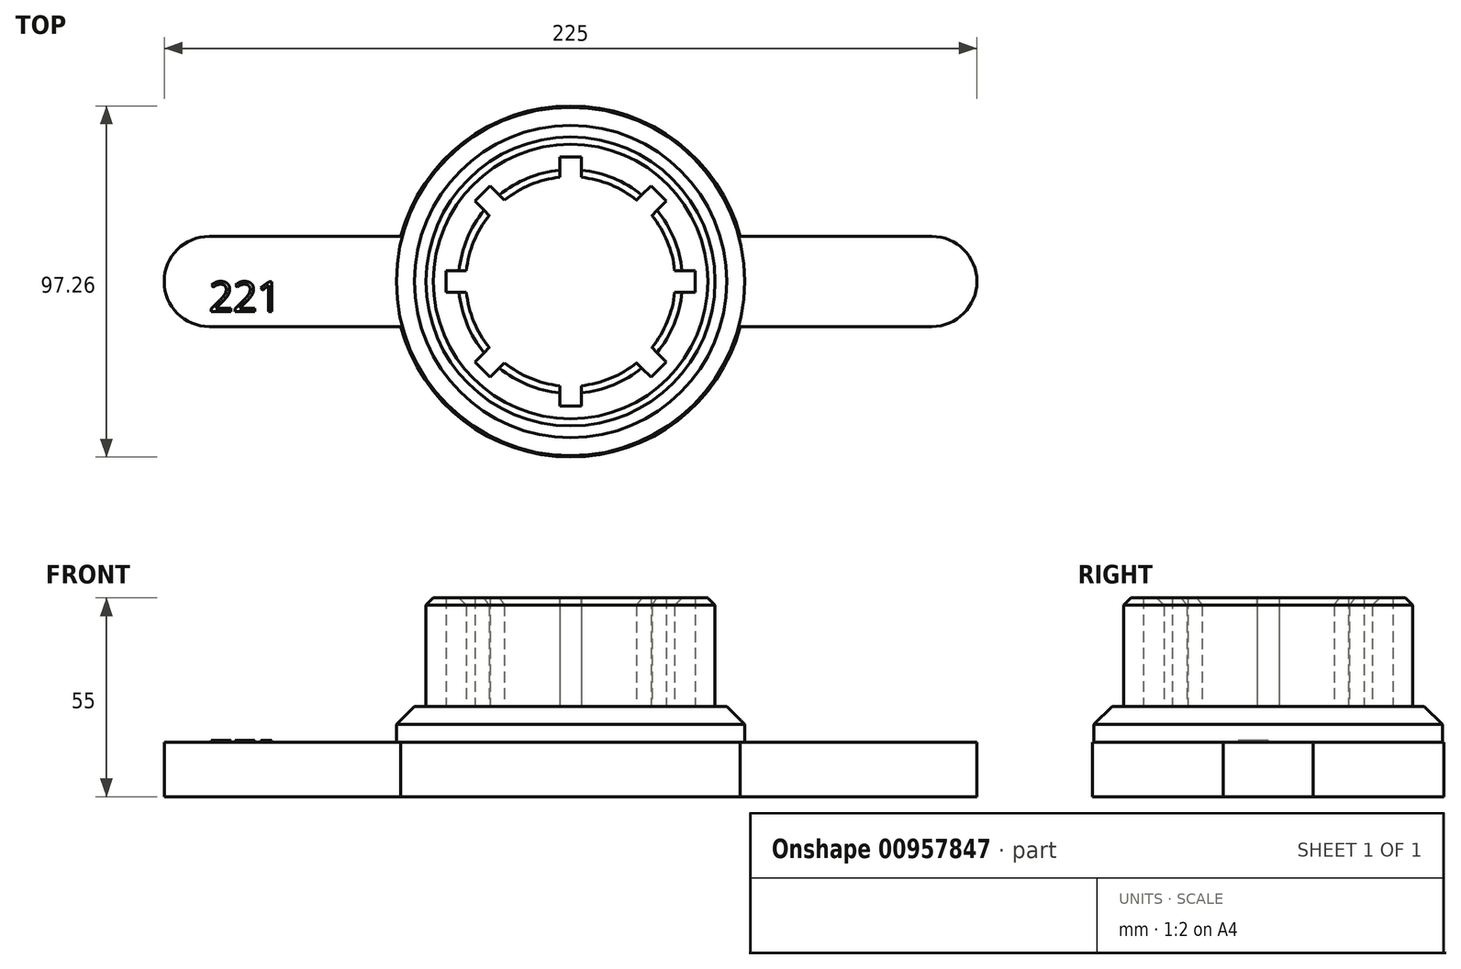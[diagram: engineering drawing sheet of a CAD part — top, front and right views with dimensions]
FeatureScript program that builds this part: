
annotation { "Feature Type Name" : "Feature", "Feature Type Description" : "" }
export const myFeature = defineFeature(function(context is Context, id is Id, definition is map)
    precondition{}
    {
        {
            var Q0;
            Q0=qCreatedBy(makeId("Top.planeOp"),FACE);
            var sketch = newSketch(context, id + "F0", { "sketchPlane" : qUnion([Q0])});
            skCircle(sketch, "E0", {"center": v(0, 0) * mm, "radius": 29 * mm});
            skPoint(sketch, "E1", {"position": v(0, 29) * mm});
            skPoint(sketch, "E2", {"position": v(0, 34.5) * mm});
            skLineSegment(sketch, "E3", {"start": v(0, 34.5) * mm, "end": v(3, 34.5) * mm});
            skLineSegment(sketch, "E4", {"start": v(3, 34.5) * mm, "end": v(3, 28.84) * mm});
            skLineSegment(sketch, "E5.MirrorCS", {"start": v(0, 34.5) * mm, "end": v(-3, 34.5) * mm});
            skLineSegment(sketch, "E6.MirrorCS", {"start": v(-3, 34.5) * mm, "end": v(-3, 28.84) * mm});
            skLineSegment(sketch, "E7.1.0", {"start": v(-26.52, 22.27) * mm, "end": v(-22.52, 18.27) * mm});
            skLineSegment(sketch, "E7.1.1", {"start": v(-24.4, 24.4) * mm, "end": v(-26.52, 22.27) * mm});
            skLineSegment(sketch, "E7.1.2", {"start": v(-24.4, 24.4) * mm, "end": v(-22.27, 26.52) * mm});
            skLineSegment(sketch, "E7.1.3", {"start": v(-22.27, 26.52) * mm, "end": v(-18.27, 22.52) * mm});
            skLineSegment(sketch, "E7.2.0", {"start": v(-34.5, -3) * mm, "end": v(-28.84, -3) * mm});
            skLineSegment(sketch, "E7.2.1", {"start": v(-34.5, 0) * mm, "end": v(-34.5, -3) * mm});
            skLineSegment(sketch, "E7.2.2", {"start": v(-34.5, 0) * mm, "end": v(-34.5, 3) * mm});
            skLineSegment(sketch, "E7.2.3", {"start": v(-34.5, 3) * mm, "end": v(-28.84, 3) * mm});
            skLineSegment(sketch, "E7.3.0", {"start": v(-22.27, -26.52) * mm, "end": v(-18.27, -22.52) * mm});
            skLineSegment(sketch, "E7.3.1", {"start": v(-24.4, -24.4) * mm, "end": v(-22.27, -26.52) * mm});
            skLineSegment(sketch, "E7.3.2", {"start": v(-24.4, -24.4) * mm, "end": v(-26.52, -22.27) * mm});
            skLineSegment(sketch, "E7.3.3", {"start": v(-26.52, -22.27) * mm, "end": v(-22.52, -18.27) * mm});
            skLineSegment(sketch, "E7.4.0", {"start": v(3, -34.5) * mm, "end": v(3, -28.84) * mm});
            skLineSegment(sketch, "E7.4.1", {"start": v(0, -34.5) * mm, "end": v(3, -34.5) * mm});
            skLineSegment(sketch, "E7.4.2", {"start": v(0, -34.5) * mm, "end": v(-3, -34.5) * mm});
            skLineSegment(sketch, "E7.4.3", {"start": v(-3, -34.5) * mm, "end": v(-3, -28.84) * mm});
            skLineSegment(sketch, "E7.5.0", {"start": v(26.52, -22.27) * mm, "end": v(22.52, -18.27) * mm});
            skLineSegment(sketch, "E7.5.1", {"start": v(24.4, -24.4) * mm, "end": v(26.52, -22.27) * mm});
            skLineSegment(sketch, "E7.5.2", {"start": v(24.4, -24.4) * mm, "end": v(22.27, -26.52) * mm});
            skLineSegment(sketch, "E7.5.3", {"start": v(22.27, -26.52) * mm, "end": v(18.27, -22.52) * mm});
            skLineSegment(sketch, "E7.6.0", {"start": v(34.5, 3) * mm, "end": v(28.84, 3) * mm});
            skLineSegment(sketch, "E7.6.1", {"start": v(34.5, 0) * mm, "end": v(34.5, 3) * mm});
            skLineSegment(sketch, "E7.6.2", {"start": v(34.5, 0) * mm, "end": v(34.5, -3) * mm});
            skLineSegment(sketch, "E7.6.3", {"start": v(34.5, -3) * mm, "end": v(28.84, -3) * mm});
            skLineSegment(sketch, "E7.7.0", {"start": v(22.27, 26.52) * mm, "end": v(18.27, 22.52) * mm});
            skLineSegment(sketch, "E7.7.1", {"start": v(24.4, 24.4) * mm, "end": v(22.27, 26.52) * mm});
            skLineSegment(sketch, "E7.7.2", {"start": v(24.4, 24.4) * mm, "end": v(26.52, 22.27) * mm});
            skLineSegment(sketch, "E7.7.3", {"start": v(26.52, 22.27) * mm, "end": v(22.52, 18.27) * mm});
            skCircle(sketch, "E8", {"center": v(0, 0) * mm, "radius": 40 * mm});
            skSolve(sketch);
        }
        {
            var Q0;
            Q0 = qSketchRegion(id + "F0", true);
            var Q1;
            Q1 = qSketchRegion(id + "F2", true);
            extrude(context, id + "F1", {"entities" : qUnion([Q0, Q1]), "depth" : 30 * mm, "offsetDistance" : 25 * mm});
        }
        {
            var Q0;
            Q0=qCreatedBy(makeId("Top.planeOp"),FACE);
            var sketch = newSketch(context, id + "F2", { "sketchPlane" : qUnion([Q0])});
            skCircle(sketch, "E9", {"center": v(0, 0) * mm, "radius": 48.23 * mm});
            skSolve(sketch);
        }
        {
            var Q0;
            Q0 = qSketchRegion(id + "F2", true);
            extrude(context, id + "F3", {"entities" : qUnion([Q0]), "operationType" : NewBodyOperationType.ADD, "oppositeDirection" : true, "depth" : 10 * mm, "offsetDistance" : 25 * mm});
        }
        {
            var Q0;
            Q0=makeQuery(id+"F3.opExtrude","CAP_FACE",FACE,{"disambiguationData":[OSD([sQuery(id+"F2.wireOp",EDGE,"E9")])],"isStart":false});
            var sketch = newSketch(context, id + "F4", { "sketchPlane" : qUnion([Q0])});
            skLineSegment(sketch, "E10.bottom", {"start": v(100, -12.5) * mm, "end": v(-100, -12.5) * mm});
            skLineSegment(sketch, "E10.top", {"start": v(100, 12.5) * mm, "end": v(-100, 12.5) * mm});
            skLineSegment(sketch, "E10.left", {"start": v(100, -12.5) * mm, "end": v(100, 12.5) * mm});
            skLineSegment(sketch, "E10.right", {"start": v(-100, -12.5) * mm, "end": v(-100, 12.5) * mm});
            skPoint(sketch, "E10.middle", {"position": v(0, 0) * mm});
            skCircle(sketch, "E11", {"center": v(-100, 0) * mm, "radius": 12.5 * mm});
            skPoint(sketch, "E11.third.point", {"position": v(-89.28, -6.44) * mm});
            skCircle(sketch, "E12.MirrorC", {"center": v(100, 0) * mm, "radius": 12.5 * mm});
            skCircle(sketch, "E13", {"center": v(0, 0) * mm, "radius": 48.63 * mm});
            skSolve(sketch);
        }
        {
            var Q0;
            Q0 = qSketchRegion(id + "F4", true);
            extrude(context, id + "F5", {"entities" : qUnion([Q0]), "operationType" : NewBodyOperationType.ADD, "depth" : 15 * mm, "offsetDistance" : 25 * mm});
        }
        {
            var Q0;
            {var subQ0=sQuery(id+"F0.wireOp",EDGE,"E0");Q0=makeQuery(id+"F1.opExtrude","CAP_EDGE",EDGE,{"disambiguationData":[OSD([subQ0]),TDD([makeQuery(id+"F0.imprint","IMPRINT",EDGE,{"disambiguationData":[TD([[makeQuery(id+"F0.imprint","INTERSECT",VERTEX,{"derivedFrom":[subQ0,sQuery(id+"F0.wireOp",EDGE,"E7.1.0")]}),-1.0]])],"derivedFrom":subQ0})])],"isStart":false});}
            var Q1;
            {var subQ0=sQuery(id+"F0.wireOp",EDGE,"E0");Q1=makeQuery(id+"F1.opExtrude","CAP_EDGE",EDGE,{"disambiguationData":[OSD([subQ0]),TDD([makeQuery(id+"F0.imprint","IMPRINT",EDGE,{"disambiguationData":[TD([[makeQuery(id+"F0.imprint","INTERSECT",VERTEX,{"derivedFrom":[subQ0,sQuery(id+"F0.wireOp",EDGE,"E7.2.0")]}),-1.0]])],"derivedFrom":subQ0})])],"isStart":false});}
            var Q2;
            {var subQ0=sQuery(id+"F0.wireOp",EDGE,"E0");Q2=makeQuery(id+"F1.opExtrude","CAP_EDGE",EDGE,{"disambiguationData":[OSD([subQ0]),TDD([makeQuery(id+"F0.imprint","IMPRINT",EDGE,{"disambiguationData":[TD([[makeQuery(id+"F0.imprint","INTERSECT",VERTEX,{"derivedFrom":[subQ0,sQuery(id+"F0.wireOp",EDGE,"E7.3.0")]}),-1.0]])],"derivedFrom":subQ0})])],"isStart":false});}
            var Q3;
            {var subQ0=sQuery(id+"F0.wireOp",EDGE,"E0");Q3=makeQuery(id+"F1.opExtrude","CAP_EDGE",EDGE,{"disambiguationData":[OSD([subQ0]),TDD([makeQuery(id+"F0.imprint","IMPRINT",EDGE,{"disambiguationData":[TD([[makeQuery(id+"F0.imprint","INTERSECT",VERTEX,{"derivedFrom":[subQ0,sQuery(id+"F0.wireOp",EDGE,"E7.4.0")]}),-1.0]])],"derivedFrom":subQ0})])],"isStart":false});}
            var Q4;
            {var subQ0=sQuery(id+"F0.wireOp",EDGE,"E0");Q4=makeQuery(id+"F1.opExtrude","CAP_EDGE",EDGE,{"disambiguationData":[OSD([subQ0]),TDD([makeQuery(id+"F0.imprint","IMPRINT",EDGE,{"disambiguationData":[TD([[makeQuery(id+"F0.imprint","INTERSECT",VERTEX,{"derivedFrom":[subQ0,sQuery(id+"F0.wireOp",EDGE,"E7.5.0")]}),-1.0]])],"derivedFrom":subQ0})])],"isStart":false});}
            var Q5;
            {var subQ0=sQuery(id+"F0.wireOp",EDGE,"E0");Q5=makeQuery(id+"F1.opExtrude","CAP_EDGE",EDGE,{"disambiguationData":[OSD([subQ0]),TDD([makeQuery(id+"F0.imprint","IMPRINT",EDGE,{"disambiguationData":[TD([[makeQuery(id+"F0.imprint","INTERSECT",VERTEX,{"derivedFrom":[subQ0,sQuery(id+"F0.wireOp",EDGE,"E7.6.0")]}),-1.0]])],"derivedFrom":subQ0})])],"isStart":false});}
            var Q6;
            {var subQ0=sQuery(id+"F0.wireOp",EDGE,"E0");Q6=makeQuery(id+"F1.opExtrude","CAP_EDGE",EDGE,{"disambiguationData":[OSD([subQ0]),TDD([makeQuery(id+"F0.imprint","IMPRINT",EDGE,{"disambiguationData":[TD([[makeQuery(id+"F0.imprint","INTERSECT",VERTEX,{"derivedFrom":[subQ0,sQuery(id+"F0.wireOp",EDGE,"E4")]}),1.0]])],"derivedFrom":subQ0})])],"isStart":false});}
            var Q7;
            {var subQ0=sQuery(id+"F0.wireOp",EDGE,"E0");Q7=makeQuery(id+"F1.opExtrude","CAP_EDGE",EDGE,{"disambiguationData":[OSD([subQ0]),TDD([makeQuery(id+"F0.imprint","IMPRINT",EDGE,{"disambiguationData":[TD([[makeQuery(id+"F0.imprint","INTERSECT",VERTEX,{"derivedFrom":[subQ0,sQuery(id+"F0.wireOp",EDGE,"E6.MirrorCS")]}),-1.0]])],"derivedFrom":subQ0})])],"isStart":false});}
            chamfer(context, id + "F6", {"entities" : qUnion([Q0, Q1, Q2, Q3, Q4, Q5, Q6, Q7]), "width" : 2 * mm, "tangentPropagation" : true});
        }
        {
            var Q0;
            Q0=makeQuery(id+"F1.opExtrude","CAP_EDGE",EDGE,{"disambiguationData":[OSD([sQuery(id+"F0.wireOp",EDGE,"E8")])],"isStart":false});
            chamfer(context, id + "F7", {"entities" : qUnion([Q0]), "width" : 2 * mm, "tangentPropagation" : true});
        }
        {
            var Q0;
            Q0=makeQuery(id+"F3.opExtrude","CAP_EDGE",EDGE,{"disambiguationData":[OSD([sQuery(id+"F2.wireOp",EDGE,"E9")])],"isStart":true});
            chamfer(context, id + "F8", {"entities" : qUnion([Q0]), "width" : 5 * mm, "tangentPropagation" : true});
        }
        {
            var Q0;
            Q0=makeQuery(id+"F5.opExtrude","CAP_FACE",FACE,{"disambiguationData":[OSD([sQuery(id+"F4.wireOp",EDGE,"E10.bottom"),sQuery(id+"F4.wireOp",EDGE,"E10.top"),sQuery(id+"F4.wireOp",EDGE,"E11"),sQuery(id+"F4.wireOp",EDGE,"E12.MirrorC"),sQuery(id+"F4.wireOp",EDGE,"E13")])],"isStart":true});
            var sketch = newSketch(context, id + "F9", { "sketchPlane" : qUnion([Q0])});
            skText(sketch, "E14", { "text": "221", "fontName": "OpenSans-Regular.ttf"});
            const initialGuessF9  = {"E14": [-0.1, -0.00832, 1, 0, 0.00832]};
            skSetInitialGuess(sketch, initialGuessF9);
            skSolve(sketch);
        }
        {
            var Q0;
            Q0 = qSketchRegion(id + "F9", true);
            extrude(context, id + "F10", {"entities" : qUnion([Q0]), "operationType" : NewBodyOperationType.ADD, "depth" : 0.5 * mm, "offsetDistance" : 25 * mm});
        }
    });
